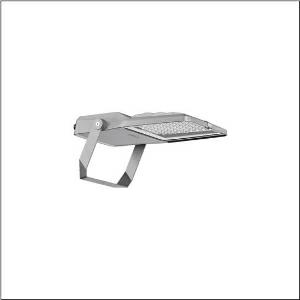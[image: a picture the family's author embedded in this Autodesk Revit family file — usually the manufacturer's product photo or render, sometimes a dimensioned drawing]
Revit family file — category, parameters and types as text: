
# Revit family: floodlight_fl_21_mini___pl33t_5xa7775d2f1a_0460
name_source: partatom
category: Lighting Fixtures
units: mm (PartAtom-declared; Revit-internal decimal feet)

## family parameters
Cut with Voids When Loaded = No
Host = Face
Light Source = No
Part Type = Normal
Room Calculation Point = No
Round Connector Dimension = Use Diameter
Shared = No

## types (1)
- --- (1 x LED, 17630 lm, 142.9 W, 3000K)
    Apparent Load = 143 VA
    CIE Flux Codes = 26 75 99 100 100
    Color Rendering = 70
    Color Temperature = 3000K
    Default Elevation = 1800 mm
    Description = Floodlight FL 21 mini, floodlight, primary light control with lens, of PMMA, primary optical cover: protective disc, of toughened safety glass, transparent, light distribution: PL33T, light emission: direct distribution, installation type: surface-mounted, LED, High Power LED, rated luminous flux: 17.630lm, luminous efficacy: 123lm/W, light colour: 730, colour temperature: 3000K, control gear: Smart Interface (Zhaga), control: flexible luminous flux parameterisation, time-dependent luminous flux control, constant luminous flux control, overheat protection, pre-setting: logarithmic dimming characteristic, with terminal, 6-pole, mains connection: 220..240V, AC, 50/60Hz, start of lifetime: 143W, end of service life: 151W, reduction: 63W, luminaire housing, of diecast aluminium, powder-coated, SITECO metallic grey (DB 702S), corrosivity category C5 mid according to DIN EN ISO 12944, suitable for swimming pools, chlorine-resistant, sealing non-destructively replaceable, mounting bracket, of steel, galvanised, powder-coated, SITECO metallic grey (DB 702S), Smart Interface above, protection rating (complete): IP66, insulation class (complete): insulation class II (safety insulation), certification: CE, ENEC, VDE, protection symbol: D, impact resistance: IK08, permissible operating ambient temperature: -40..+40°C, permissible operating ambient temperature for outdoor applications: -40..+50°C, standard: DIN EN 12944, LABS conformity tested according to VDMA 24364:2018-05, packaging unit: 1 piece

Light Distribution: PL33T
    Height = 70 mm
    Lamp = 1 x LED
    Lamp Light Flux = 17630 lm
    Lamp Power = 142.9 W
    Lamp count = 1
    Length = 485 mm
    Luminous efficacy = 123 lm/W
    Manufacturer = Siteco
    ModVariant = No
    Model = 5XA7775D2F1A
    Number of Poles = 1
    OnlyDefault = Yes
    Power Factor = 1
    Product Name = Floodlight FL 21 mini | PL33T
    Product group = floodlight | pylon annexe
    ProductGroupID = 6201
    Protection Class = Protection class II
    Protection Degree = IP 66
    RLX_Detail_Level = 1
    RLX_Emergency_Light_Flux = 0 lm
    RLX_Emergency_Type = 0
    RLX_Emergency_Type_DB = No
    RlxData = <blob elided: 96041 chars, md5=48c05599>
    Socket = socket
    Standby Power = 0 W
    System Light Flux = 17630 lm
    System Power = 143 W
    Type Comments = factory setting: luminous flux: 100 % | dim-lin: 254 | 730 mA
    Type Image = l_1006845.jpg
    URL = http://relux.com
    VarID = @adj_147929
    Voltage = 0 V
    Weight = 0.00 kg
    Width = 337 mm

## geometry (parser evidence)
native form markers: Blend x4, Sweep x14
no freeform markers — native parametric forms only
